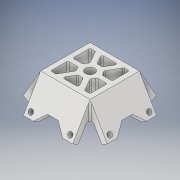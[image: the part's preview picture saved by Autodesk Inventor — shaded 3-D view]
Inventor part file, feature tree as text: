
AUTODESK INVENTOR PART (.ipt)
format: ipt  version: 2019 (Build 230136000, 136)  size: 381,952 bytes
history: native  units: in
note: dims shown in document units (in); Inventor stores cm internally (conversion verified against a paired STEP export)
features: sketch x7, extrude x6, fillet x3, pattern_circular x2, hole x1, plane x1
ambient origin geometry x8: Origin, YZ Plane, XZ Plane, XY Plane, X Axis, Y Axis, Z Axis, Center Point
bodies: Solid1 (feature_tree)
feature tree (20):
  extrude  "Extrusion1"  Depth=2.0in
  pattern_circular  "Circular Pattern1"  Count=4 Angle=360.0deg
  hole  "Hole1"  [1 undecoded]
  extrude  "Extrusion3"  Depth=0.0625in
  extrude  "Extrusion4"  Depth=0.0625in
  extrude  "Extrusion5"  Depth=0.0625in
  fillet  "Fillet1"  Radius=0.25in
  pattern_circular  "Circular Pattern2"  [2 undecoded]
  fillet  "Fillet2"  Radius=0.3in
  extrude  "Extrusion6"  Depth=0.0625in TaperAngle=0.0deg
  plane  "Work Plane1"
  extrude  "Extrusion8"  TaperAngle=45.0deg  [1 undecoded]
  fillet  "Fillet3"  Radius=0.4in
  sketch  "Sketch2"  dims[d2=3.0in d3=2.0in]
  sketch  "Sketch5"  dims[d4=0.5in]
  sketch  "Sketch6"  dims[d5=30.0deg]
  sketch  "Sketch7"  dims[d6=4.5in]
  sketch  "Sketch8"  dims[d7=1.4in]
  sketch  "Sketch9"  dims[d8=2.0in d9=0.0in d10=1.5748in d11=360.0deg]
  sketch  "Sketch11"  dims[d17=1.5748in d18=360.0deg d20=1.6in d21=0.201in d22=0.201in d24=1.2in d25=0.203in d26=0.75in d27=0.375in d28=0.25in d29=0.5635in d30=1.0in d31=0.8108in d32=0.25in d34=0.25in d35=0.3in d36=0.2in d37=0.0in d38=45.0deg d39=0.4in d40=0.25in d41=0.0in d42=0.377in d44=0.25in d45=0.0in d46=1.6in d47=1.6in d48=0.2in d49=0.2in d50=0.2in d51=0.75in d52=0.0625in d53=0.0625in d54=0.5in d55=0.25in d56=0.0in d60=45.0deg d61=0.0625in d62=0.625in d63=0.0in d64=0.0625in]
note: 4 required parameter values undecoded (feature->parameter linkage not recoverable at this tier; creation-order binding heuristic only, values carry confidence <= 0.55)
